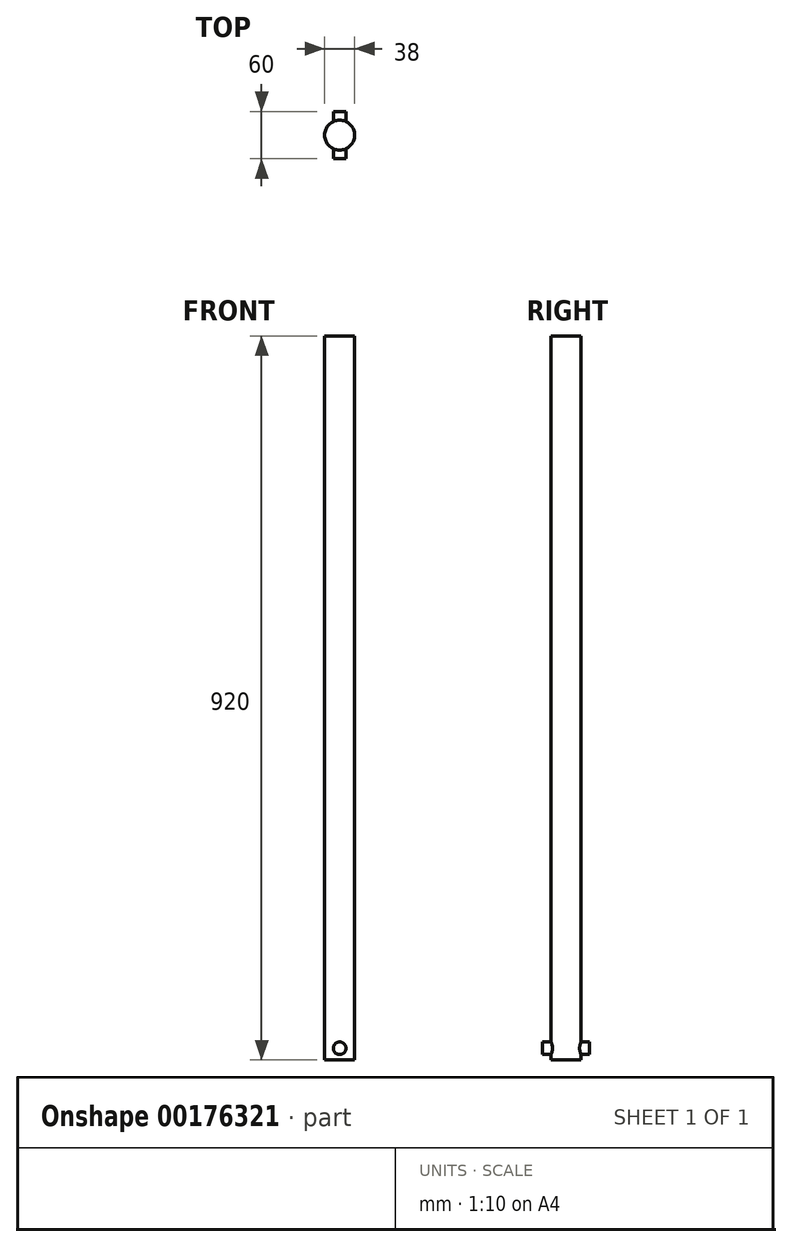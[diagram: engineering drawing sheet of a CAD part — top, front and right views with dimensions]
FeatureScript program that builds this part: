
annotation { "Feature Type Name" : "Feature", "Feature Type Description" : "" }
export const myFeature = defineFeature(function(context is Context, id is Id, definition is map)
    precondition{}
    {
        {
            var Q0;
            Q0=qCreatedBy(makeId("Top.planeOp"),FACE);
            var sketch = newSketch(context, id + "F0", { "sketchPlane" : qUnion([Q0])});
            skCircle(sketch, "E0", {"center": v(0, 0) * mm, "radius": 19 * mm});
            skSolve(sketch);
        }
        {
            var Q0;
            Q0=makeQuery(id+"F0.imprint","IMPRINT",FACE,{"disambiguationData":[TD([[makeQuery(id+"F0.imprint","IMPRINT",EDGE,{"derivedFrom":sQuery(id+"F0.wireOp",EDGE,"E0")}),1.0]])]});
            extrude(context, id + "F1", {"entities" : qUnion([Q0]), "depth" : 920 * mm});
        }
        {
            var Q0;
            Q0=qCreatedBy(makeId("Front.planeOp"),FACE);
            var sketch = newSketch(context, id + "F2", { "sketchPlane" : qUnion([Q0])});
            skCircle(sketch, "E1", {"center": v(0, 15) * mm, "radius": 8 * mm});
            skLineSegment(sketch, "E2", {"start": v(0, 15) * mm, "end": v(0, 0) * mm, "construction": true});
            skSolve(sketch);
        }
        {
            var Q0;
            Q0 = qSketchRegion(id + "F2", true);
            extrude(context, id + "F3", {"entities" : qUnion([Q0]), "operationType" : NewBodyOperationType.ADD, "endBound" : BoundingType.SYMMETRIC, "depth" : 60 * mm});
        }
    });
